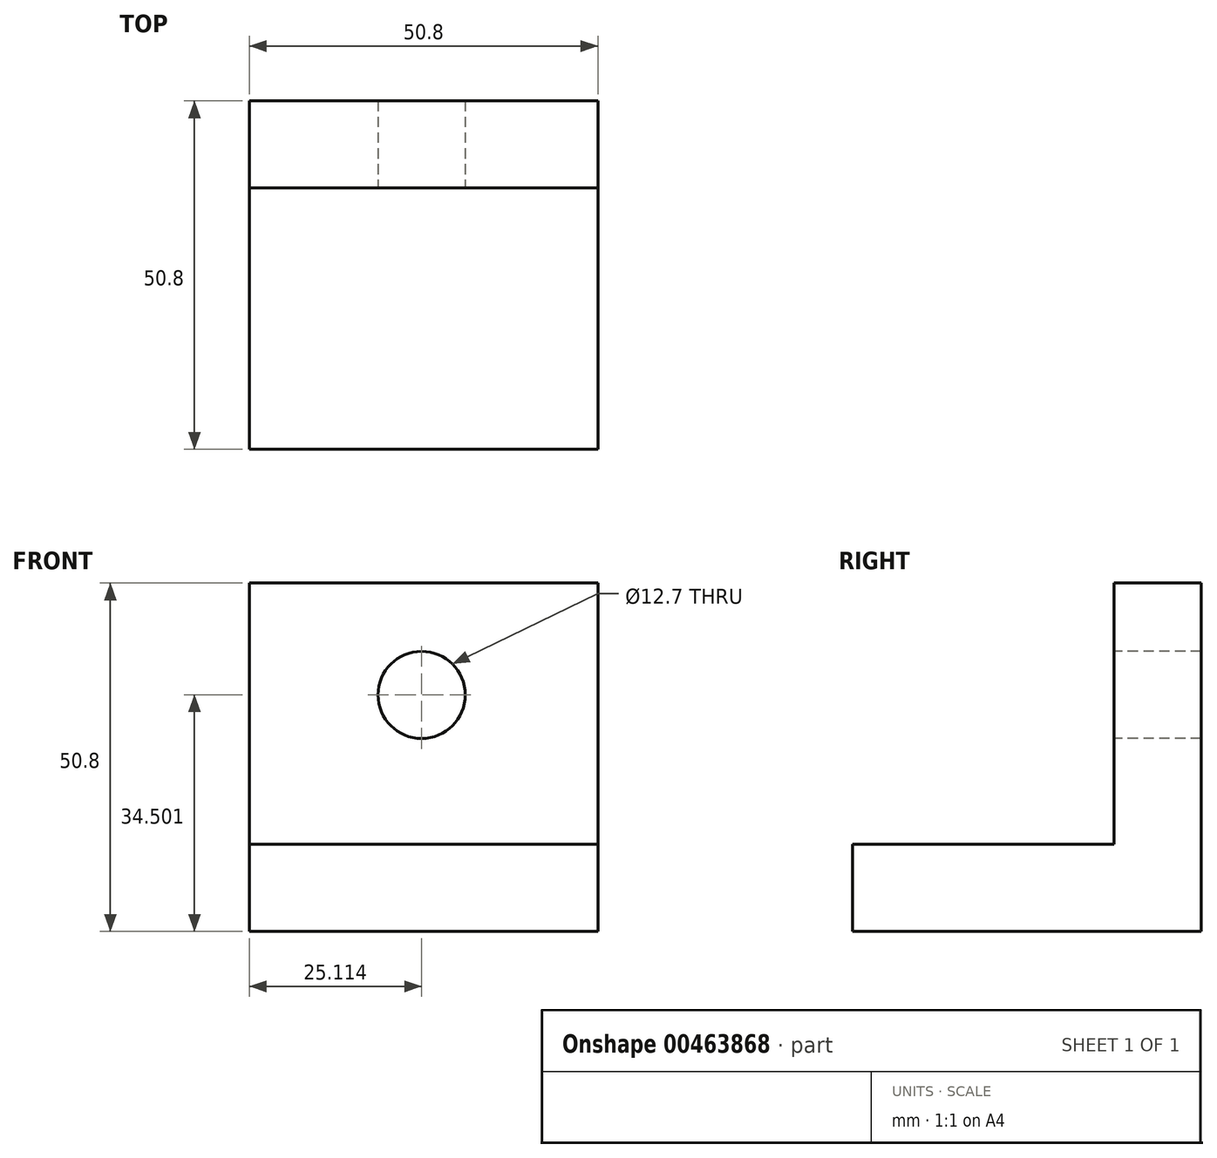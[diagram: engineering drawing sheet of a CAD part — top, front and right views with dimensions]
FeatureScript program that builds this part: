
annotation { "Feature Type Name" : "Feature", "Feature Type Description" : "" }
export const myFeature = defineFeature(function(context is Context, id is Id, definition is map)
    precondition{}
    {
        {
            var Q0;
            Q0=qCreatedBy(makeId("Right.planeOp"),FACE);
            var sketch = newSketch(context, id + "F0", { "sketchPlane" : qUnion([Q0])});
            skLineSegment(sketch, "E0.bottom", {"start": v(0, 13.41) * mm, "end": v(12.7, 13.41) * mm});
            skLineSegment(sketch, "E0.top", {"start": v(0, -37.39) * mm, "end": v(12.7, -37.39) * mm});
            skLineSegment(sketch, "E0.left", {"start": v(0, 13.41) * mm, "end": v(0, -37.39) * mm});
            skLineSegment(sketch, "E0.right", {"start": v(12.7, 13.41) * mm, "end": v(12.7, -37.39) * mm});
            skLineSegment(sketch, "E1.bottom", {"start": v(0, -24.69) * mm, "end": v(-38.1, -24.69) * mm});
            skLineSegment(sketch, "E1.top", {"start": v(0, -37.39) * mm, "end": v(-38.1, -37.39) * mm});
            skLineSegment(sketch, "E1.left", {"start": v(0, -24.69) * mm, "end": v(0, -37.39) * mm});
            skLineSegment(sketch, "E1.right", {"start": v(-38.1, -24.69) * mm, "end": v(-38.1, -37.39) * mm});
            skSolve(sketch);
        }
        {
            var Q0;
            Q0=makeQuery(id+"F0.imprint","IMPRINT",FACE,{"disambiguationData":[TD([[makeQuery(id+"F0.imprint","IMPRINT",EDGE,{"derivedFrom":sQuery(id+"F0.wireOp",EDGE,"E0.bottom")}),-1.0]])]});
            var Q1;
            Q1=makeQuery(id+"F0.imprint","IMPRINT",FACE,{"disambiguationData":[TD([[makeQuery(id+"F0.imprint","IMPRINT",EDGE,{"derivedFrom":sQuery(id+"F0.wireOp",EDGE,"E1.bottom")}),1.0]])]});
            extrude(context, id + "F1", {"entities" : qUnion([Q0, Q1]), "depth" : 50.8 * mm});
        }
        {
            var Q0;
            Q0=qCreatedBy(makeId("Front.planeOp"),FACE);
            var sketch = newSketch(context, id + "F2", { "sketchPlane" : qUnion([Q0])});
            skCircle(sketch, "E2", {"center": v(25.11, -2.89) * mm, "radius": 6.35 * mm});
            skSolve(sketch);
        }
        {
            var Q0;
            Q0 = qSketchRegion(id + "F2", true);
            extrude(context, id + "F3", {"entities" : qUnion([Q0]), "operationType" : NewBodyOperationType.REMOVE, "oppositeDirection" : true, "depth" : 25.4 * mm});
        }
    });
